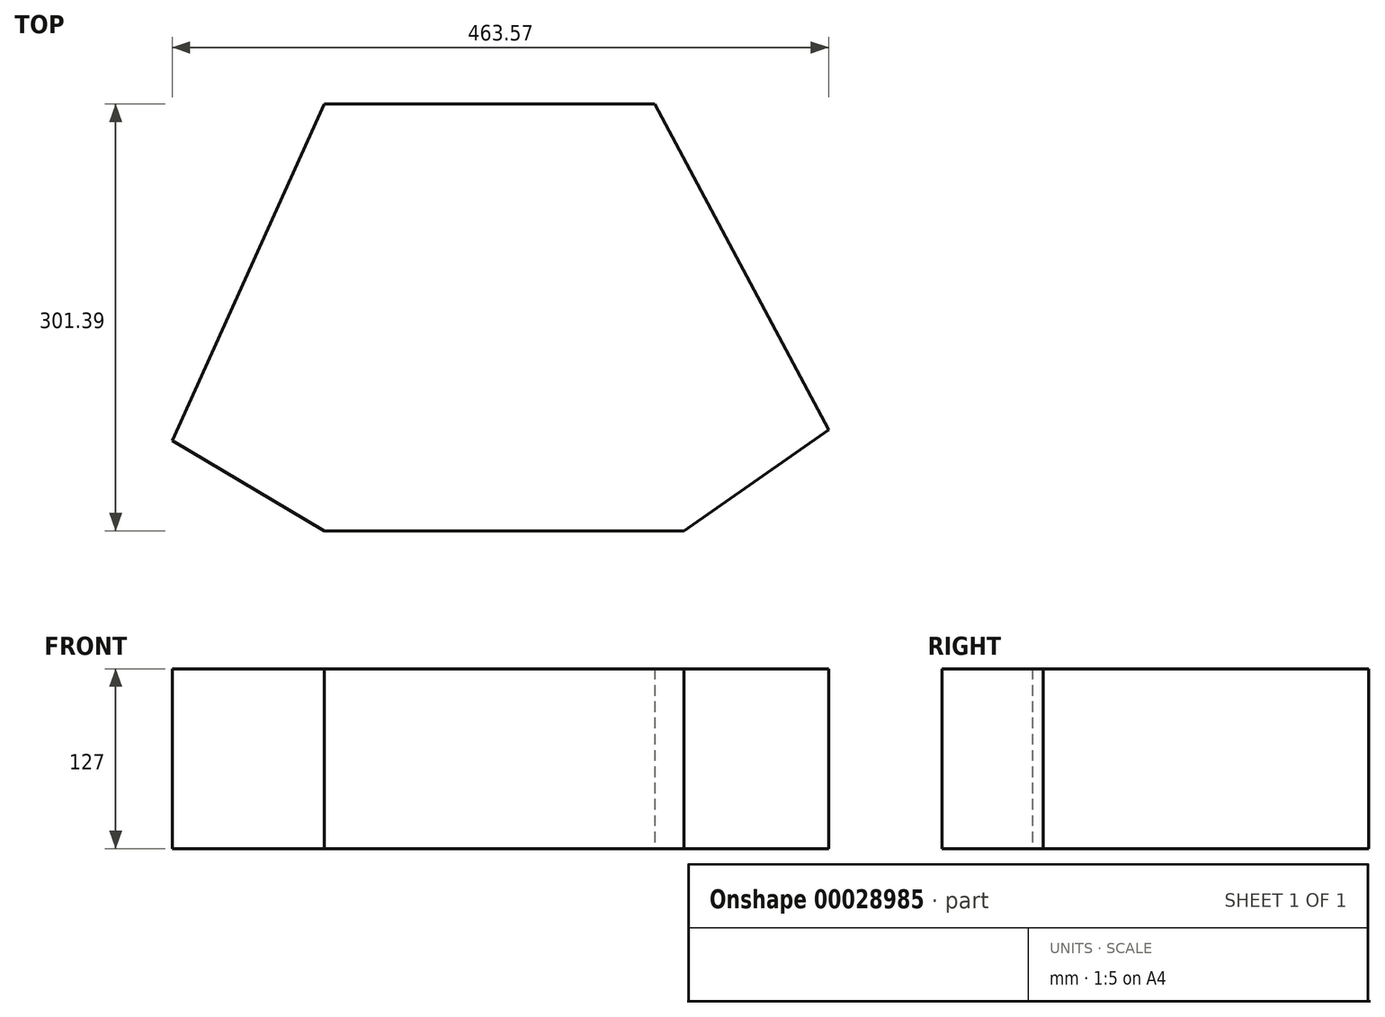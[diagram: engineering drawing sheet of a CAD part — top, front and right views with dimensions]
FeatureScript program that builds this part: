
annotation { "Feature Type Name" : "Feature", "Feature Type Description" : "" }
export const myFeature = defineFeature(function(context is Context, id is Id, definition is map)
    precondition{}
    {
        {
            var Q0;
            Q0=qCreatedBy(makeId("Top.planeOp"),FACE);
            var sketch = newSketch(context, id + "F0", { "sketchPlane" : qUnion([Q0])});
            skLineSegment(sketch, "E0", {"start": v(0, 0) * mm, "end": v(254, 0) * mm});
            skLineSegment(sketch, "E1", {"start": v(254, 0) * mm, "end": v(356.32, 71.43) * mm});
            skLineSegment(sketch, "E2", {"start": v(356.32, 71.43) * mm, "end": v(233.53, 301.39) * mm});
            skLineSegment(sketch, "E3", {"start": v(233.53, 301.39) * mm, "end": v(0, 301.39) * mm});
            skLineSegment(sketch, "E4", {"start": v(0, 301.39) * mm, "end": v(-107.25, 63.79) * mm});
            skLineSegment(sketch, "E5", {"start": v(-107.25, 63.79) * mm, "end": v(0, 0) * mm});
            skSolve(sketch);
        }
        {
            var Q0;
            Q0=makeQuery(id+"F0.imprint","IMPRINT",FACE,{"disambiguationData":[TD([[makeQuery(id+"F0.imprint","IMPRINT",EDGE,{"derivedFrom":sQuery(id+"F0.wireOp",EDGE,"E0")}),1.0]])]});
            extrude(context, id + "F1", {"entities" : qUnion([Q0]), "depth" : 127 * mm});
        }
    });
